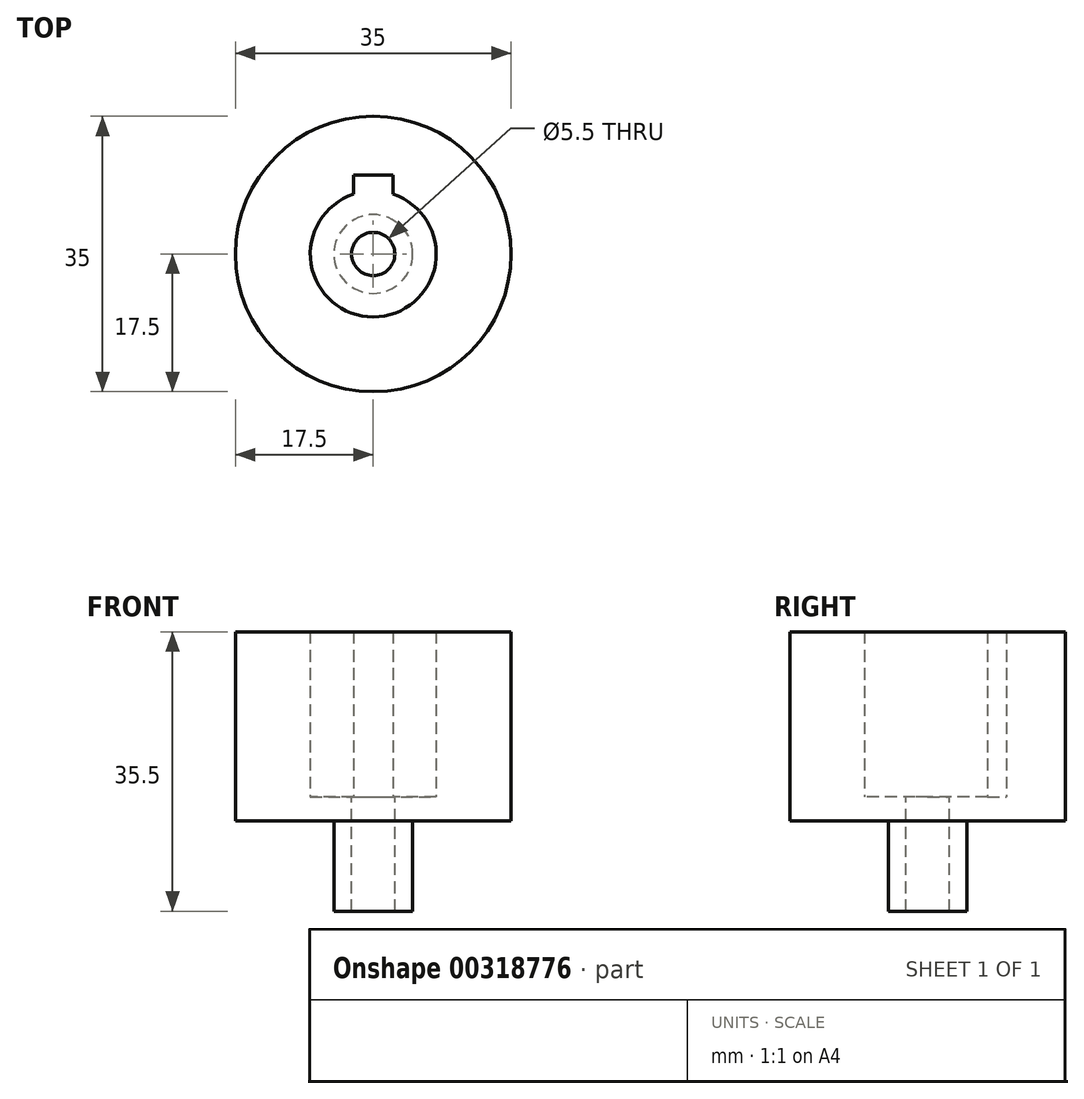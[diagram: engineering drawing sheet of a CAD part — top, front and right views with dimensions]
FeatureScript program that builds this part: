
annotation { "Feature Type Name" : "Feature", "Feature Type Description" : "" }
export const myFeature = defineFeature(function(context is Context, id is Id, definition is map)
    precondition{}
    {
        {
            var Q0;
            Q0=qCreatedBy(makeId("Top.planeOp"),FACE);
            var sketch = newSketch(context, id + "F0", { "sketchPlane" : qUnion([Q0])});
            skArc(sketch, "E0", {"start": v(-2.5, 7.6) * mm, "mid": v(0, -8) * mm, "end": v(2.5, 7.6) * mm});
            skCircle(sketch, "E1", {"center": v(0, 0) * mm, "radius": 17.5 * mm});
            skLineSegment(sketch, "E2.top", {"start": v(-2.5, 10) * mm, "end": v(2.5, 10) * mm});
            skLineSegment(sketch, "E2.left", {"start": v(-2.5, 7.6) * mm, "end": v(-2.5, 10) * mm});
            skLineSegment(sketch, "E2.right", {"start": v(2.5, 7.6) * mm, "end": v(2.5, 10) * mm});
            skPoint(sketch, "E3.orphan", {"position": v(2.5, 0) * mm});
            skPoint(sketch, "E2.bottom.start.orphan", {"position": v(-2.5, 0) * mm});
            skSolve(sketch);
        }
        {
            var Q0;
            Q0=makeQuery(id+"F0.imprint","IMPRINT",FACE,{"disambiguationData":[TD([[makeQuery(id+"F0.imprint","IMPRINT",EDGE,{"derivedFrom":sQuery(id+"F0.wireOp",EDGE,"E0")}),-1.0]])]});
            extrude(context, id + "F1", {"entities" : qUnion([Q0]), "depth" : 21 * mm, "hasSecondDirection" : true, "secondDirectionOppositeDirection" : true, "secondDirectionDepth" : 25 * mm, "offsetDistance" : 25 * mm, "symmetric" : true});
        }
        {
            var Q0;
            Q0=makeQuery(id+"F1.opExtrude","CAP_FACE",FACE,{"disambiguationData":[OSD([sQuery(id+"F0.wireOp",EDGE,"E0"),sQuery(id+"F0.wireOp",EDGE,"E1"),sQuery(id+"F0.wireOp",EDGE,"E2.top"),sQuery(id+"F0.wireOp",EDGE,"E2.left"),sQuery(id+"F0.wireOp",EDGE,"E2.right")])],"isStart":true});
            var sketch = newSketch(context, id + "F2", { "sketchPlane" : qUnion([Q0])});
            skCircle(sketch, "E4", {"center": v(0, 0) * mm, "radius": 17.5 * mm});
            skSolve(sketch);
        }
        {
            var Q0;
            Q0=makeQuery(id+"F2.imprint","IMPRINT",FACE,{"disambiguationData":[TD([[makeQuery(id+"F2.imprint","IMPRINT",EDGE,{"derivedFrom":sQuery(id+"F2.wireOp",EDGE,"E4")}),-1.0]])]});
            var Q1;
            Q1=makeQuery(id+"F2.imprint","IMPRINT",FACE,{"disambiguationData":[TD([[makeQuery(id+"F2.imprint","IMPRINT",EDGE,{"derivedFrom":makeQuery(id+"F1.opExtrude","CAP_EDGE",EDGE,{"disambiguationData":[OSD([sQuery(id+"F0.wireOp",EDGE,"E0")])],"isStart":true})}),-1.0]])]});
            extrude(context, id + "F3", {"entities" : qUnion([Q0, Q1]), "operationType" : NewBodyOperationType.ADD, "offsetDistance" : 25 * mm, "depth" : 3 * mm});
        }
        {
            var Q0;
            Q0=makeQuery(id+"F3.opExtrude","CAP_FACE",FACE,{"disambiguationData":[OSD([sQuery(id+"F2.wireOp",EDGE,"E4"),sQuery(id+"F2.wireOp",EDGE,"228Es8O6-mDYL-LEw1-QSJL-FjczAlpEgmjM")])],"isStart":false});
            var sketch = newSketch(context, id + "F4", { "sketchPlane" : qUnion([Q0])});
            skCircle(sketch, "E5", {"center": v(0, 0) * mm, "radius": 5 * mm});
            skSolve(sketch);
        }
        {
            var Q0;
            Q0=makeQuery(id+"F4.imprint","IMPRINT",FACE,{"disambiguationData":[TD([[makeQuery(id+"F4.imprint","IMPRINT",EDGE,{"derivedFrom":sQuery(id+"F4.wireOp",EDGE,"E5")}),1.0]])]});
            extrude(context, id + "F5", {"entities" : qUnion([Q0]), "operationType" : NewBodyOperationType.ADD, "depth" : 11.5 * mm, "offsetDistance" : 25 * mm});
        }
        {
            var Q0;
            Q0=makeQuery(id+"F5.opExtrude","CAP_FACE",FACE,{"disambiguationData":[OSD([sQuery(id+"F4.wireOp",EDGE,"E5")])],"isStart":false});
            var sketch = newSketch(context, id + "F6", { "sketchPlane" : qUnion([Q0])});
            skCircle(sketch, "E6", {"center": v(0, 0) * mm, "radius": 1.13 * mm});
            skSolve(sketch);
        }
        {
            var Q0;
            Q0=sQuery(id+"F6.wireOp",VERTEX,"E6.center");
            var Q1;
            Q1=makeQuery(id+"F1.opExtrude","SWEPT_BODY",BODY,{"disambiguationData":[OSD([sQuery(id+"F0.wireOp",EDGE,"E0"),sQuery(id+"F0.wireOp",EDGE,"E1"),sQuery(id+"F0.wireOp",EDGE,"E2.top"),sQuery(id+"F0.wireOp",EDGE,"E2.left"),sQuery(id+"F0.wireOp",EDGE,"E2.right")])]});
            hole(context, id + "F7", {"style" : HoleStyle.SIMPLE, "endStyle" : HoleEndStyle.BLIND, "holeDiameter" : 5.5 * mm, "majorDiameter" : 5 * mm, "holeDepth" : 30 * mm, "tappedDepth" : 12 * mm, "tapClearance" : 3, "locations" : qUnion([Q0]), "scope" : qUnion([Q1])});
        }
    });
